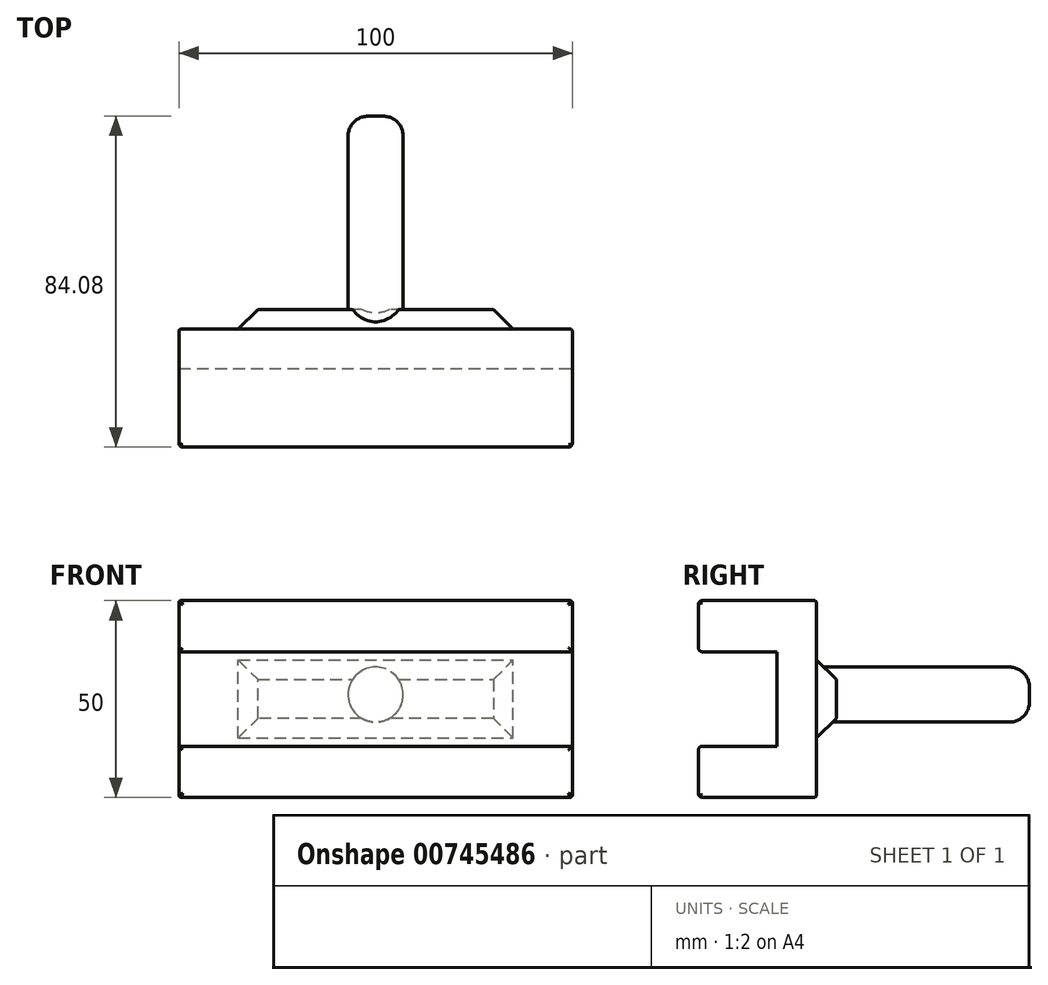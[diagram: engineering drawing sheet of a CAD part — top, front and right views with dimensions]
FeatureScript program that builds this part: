
annotation { "Feature Type Name" : "Feature", "Feature Type Description" : "" }
export const myFeature = defineFeature(function(context is Context, id is Id, definition is map)
    precondition{}
    {
        {
            var Q0;
            Q0=qCreatedBy(makeId("Front.planeOp"),FACE);
            var sketch = newSketch(context, id + "F0", { "sketchPlane" : qUnion([Q0])});
            skLineSegment(sketch, "E0.bottom", {"start": v(0, 0) * mm, "end": v(100, 0) * mm});
            skLineSegment(sketch, "E0.top", {"start": v(0, 50) * mm, "end": v(100, 50) * mm});
            skLineSegment(sketch, "E0.left", {"start": v(0, 0) * mm, "end": v(0, 50) * mm});
            skLineSegment(sketch, "E0.right", {"start": v(100, 0) * mm, "end": v(100, 50) * mm});
            skSolve(sketch);
        }
        {
            var Q0;
            Q0 = qSketchRegion(id + "F0", true);
            extrude(context, id + "F1", {"entities" : qUnion([Q0]), "depth" : 10 * mm, "offsetDistance" : 25.4 * mm});
        }
        {
            var Q0;
            Q0=makeQuery(id+"F1.opExtrude","CAP_FACE",FACE,{"disambiguationData":[OSD([sQuery(id+"F0.wireOp",EDGE,"E0.bottom"),sQuery(id+"F0.wireOp",EDGE,"E0.top"),sQuery(id+"F0.wireOp",EDGE,"E0.left"),sQuery(id+"F0.wireOp",EDGE,"E0.right")])],"isStart":false});
            var sketch = newSketch(context, id + "F2", { "sketchPlane" : qUnion([Q0])});
            skLineSegment(sketch, "E1.bottom", {"start": v(0, 50) * mm, "end": v(100, 50) * mm});
            skLineSegment(sketch, "E1.top", {"start": v(0, 37) * mm, "end": v(100, 37) * mm});
            skLineSegment(sketch, "E1.left", {"start": v(0, 50) * mm, "end": v(0, 37) * mm});
            skLineSegment(sketch, "E1.right", {"start": v(100, 50) * mm, "end": v(100, 37) * mm});
            skSolve(sketch);
        }
        {
            var Q0;
            Q0 = qSketchRegion(id + "F2", true);
            extrude(context, id + "F3", {"entities" : qUnion([Q0]), "operationType" : NewBodyOperationType.ADD, "depth" : 20 * mm, "offsetDistance" : 25.4 * mm});
        }
        {
            var Q0;
            Q0=makeQuery(id+"F1.opExtrude","CAP_FACE",FACE,{"disambiguationData":[OSD([sQuery(id+"F0.wireOp",EDGE,"E0.bottom"),sQuery(id+"F0.wireOp",EDGE,"E0.top"),sQuery(id+"F0.wireOp",EDGE,"E0.left"),sQuery(id+"F0.wireOp",EDGE,"E0.right")])],"isStart":false});
            var sketch = newSketch(context, id + "F4", { "sketchPlane" : qUnion([Q0])});
            skLineSegment(sketch, "E2.bottom", {"start": v(0, 0) * mm, "end": v(100, 0) * mm});
            skLineSegment(sketch, "E2.top", {"start": v(0, 13) * mm, "end": v(100, 13) * mm});
            skLineSegment(sketch, "E2.left", {"start": v(0, 0) * mm, "end": v(0, 13) * mm});
            skLineSegment(sketch, "E2.right", {"start": v(100, 0) * mm, "end": v(100, 13) * mm});
            skSolve(sketch);
        }
        {
            var Q0;
            Q0 = qSketchRegion(id + "F4", true);
            extrude(context, id + "F5", {"entities" : qUnion([Q0]), "operationType" : NewBodyOperationType.ADD, "depth" : 20 * mm, "offsetDistance" : 25.4 * mm});
        }
        {
            var Q0;
            Q0=makeQuery(id+"F1.opExtrude","CAP_FACE",FACE,{"disambiguationData":[OSD([sQuery(id+"F0.wireOp",EDGE,"E0.bottom"),sQuery(id+"F0.wireOp",EDGE,"E0.top"),sQuery(id+"F0.wireOp",EDGE,"E0.left"),sQuery(id+"F0.wireOp",EDGE,"E0.right")])],"isStart":true});
            var sketch = newSketch(context, id + "F6", { "sketchPlane" : qUnion([Q0])});
            skLineSegment(sketch, "E3.bottom", {"start": v(-85, 35) * mm, "end": v(-15, 35) * mm});
            skLineSegment(sketch, "E3.top", {"start": v(-85, 15) * mm, "end": v(-15, 15) * mm});
            skLineSegment(sketch, "E3.left", {"start": v(-85, 35) * mm, "end": v(-85, 15) * mm});
            skLineSegment(sketch, "E3.right", {"start": v(-15, 35) * mm, "end": v(-15, 15) * mm});
            skSolve(sketch);
        }
        {
            var Q0;
            Q0 = qSketchRegion(id + "F6", true);
            extrude(context, id + "F7", {"entities" : qUnion([Q0]), "operationType" : NewBodyOperationType.ADD, "depth" : 5 * mm, "offsetDistance" : 25.4 * mm});
        }
        {
            var Q0;
            Q0=makeQuery(id+"F7.opExtrude","CAP_FACE",FACE,{"disambiguationData":[OSD([sQuery(id+"F6.wireOp",EDGE,"E3.bottom"),sQuery(id+"F6.wireOp",EDGE,"E3.top"),sQuery(id+"F6.wireOp",EDGE,"E3.left"),sQuery(id+"F6.wireOp",EDGE,"E3.right")])],"isStart":false});
            var sketch = newSketch(context, id + "F8", { "sketchPlane" : qUnion([Q0])});
            skCircle(sketch, "E4", {"center": v(-50, 26.12) * mm, "radius": 7 * mm});
            skSolve(sketch);
        }
        {
            var Q0;
            Q0=makeQuery(id+"F8.imprint","IMPRINT",FACE,{"disambiguationData":[TD([[makeQuery(id+"F8.imprint","IMPRINT",EDGE,{"derivedFrom":sQuery(id+"F8.wireOp",EDGE,"E4")}),1.0]])]});
            extrude(context, id + "F9", {"entities" : qUnion([Q0]), "operationType" : NewBodyOperationType.ADD, "depth" : 49.08 * mm, "offsetDistance" : 25.4 * mm});
        }
        {
            var Q0;
            Q0=makeQuery(id+"F7.opExtrude","CAP_EDGE",EDGE,{"disambiguationData":[OSD([sQuery(id+"F6.wireOp",EDGE,"E3.top")])],"isStart":false});
            var Q1;
            Q1=makeQuery(id+"F7.opExtrude","CAP_EDGE",EDGE,{"disambiguationData":[OSD([sQuery(id+"F6.wireOp",EDGE,"E3.left")])],"isStart":false});
            var Q2;
            Q2=makeQuery(id+"F7.opExtrude","CAP_EDGE",EDGE,{"disambiguationData":[OSD([sQuery(id+"F6.wireOp",EDGE,"E3.bottom")])],"isStart":false});
            var Q3;
            Q3=makeQuery(id+"F7.opExtrude","CAP_EDGE",EDGE,{"disambiguationData":[OSD([sQuery(id+"F6.wireOp",EDGE,"E3.right")])],"isStart":false});
            chamfer(context, id + "F10", {"entities" : qUnion([Q0, Q1, Q2, Q3]), "width" : 5.08 * mm, "tangentPropagation" : true});
        }
        {
            var Q0;
            Q0=makeQuery(id+"F5.opExtrude","CAP_FACE",FACE,{"disambiguationData":[OSD([sQuery(id+"F4.wireOp",EDGE,"E2.bottom"),sQuery(id+"F4.wireOp",EDGE,"E2.top"),sQuery(id+"F4.wireOp",EDGE,"E2.left"),sQuery(id+"F4.wireOp",EDGE,"E2.right")])],"isStart":false});
            var Q1;
            Q1=makeQuery(id+"F3.opExtrude","CAP_FACE",FACE,{"disambiguationData":[OSD([sQuery(id+"F2.wireOp",EDGE,"E1.bottom"),sQuery(id+"F2.wireOp",EDGE,"E1.top"),sQuery(id+"F2.wireOp",EDGE,"E1.left"),sQuery(id+"F2.wireOp",EDGE,"E1.right")])],"isStart":false});
            fillet(context, id + "F11", {"entities" : qUnion([Q0, Q1]), "radius" : 1 * mm, "tangentPropagation" : true, "allowEdgeOverflow" : false});
        }
        {
            var Q0;
            Q0=makeQuery(id+"F5.boolean.opBoolean","MERGE",EDGE,{"derivedFrom":[makeQuery(id+"F1.opExtrude","SWEPT_EDGE",EDGE,{"disambiguationData":[OSD([sQuery(id+"F0.wireOp",EDGE,"E0.bottom"),sQuery(id+"F0.wireOp",EDGE,"E0.left")])]}),makeQuery(id+"F5.opExtrude","SWEPT_EDGE",EDGE,{"disambiguationData":[OSD([sQuery(id+"F4.wireOp",EDGE,"E2.bottom"),sQuery(id+"F4.wireOp",EDGE,"E2.left")])]})]});
            var Q1;
            Q1=makeQuery(id+"F3.boolean.opBoolean","MERGE",EDGE,{"derivedFrom":[makeQuery(id+"F1.opExtrude","SWEPT_EDGE",EDGE,{"disambiguationData":[OSD([sQuery(id+"F0.wireOp",EDGE,"E0.top"),sQuery(id+"F0.wireOp",EDGE,"E0.left")])]}),makeQuery(id+"F3.opExtrude","SWEPT_EDGE",EDGE,{"disambiguationData":[OSD([sQuery(id+"F2.wireOp",EDGE,"E1.bottom"),sQuery(id+"F2.wireOp",EDGE,"E1.left")])]})]});
            var Q2;
            Q2=makeQuery(id+"F1.opExtrude","CAP_EDGE",EDGE,{"disambiguationData":[OSD([sQuery(id+"F0.wireOp",EDGE,"E0.left")])],"isStart":true});
            var Q3;
            Q3=makeQuery(id+"F1.opExtrude","CAP_EDGE",EDGE,{"disambiguationData":[OSD([sQuery(id+"F0.wireOp",EDGE,"E0.bottom")])],"isStart":true});
            var Q4;
            Q4=makeQuery(id+"F5.boolean.opBoolean","MERGE",EDGE,{"derivedFrom":[makeQuery(id+"F1.opExtrude","SWEPT_EDGE",EDGE,{"disambiguationData":[OSD([sQuery(id+"F0.wireOp",EDGE,"E0.bottom"),sQuery(id+"F0.wireOp",EDGE,"E0.right")])]}),makeQuery(id+"F5.opExtrude","SWEPT_EDGE",EDGE,{"disambiguationData":[OSD([sQuery(id+"F4.wireOp",EDGE,"E2.bottom"),sQuery(id+"F4.wireOp",EDGE,"E2.right")])]})]});
            var Q5;
            Q5=makeQuery(id+"F1.opExtrude","CAP_EDGE",EDGE,{"disambiguationData":[OSD([sQuery(id+"F0.wireOp",EDGE,"E0.right")])],"isStart":true});
            var Q6;
            Q6=makeQuery(id+"F3.boolean.opBoolean","MERGE",EDGE,{"derivedFrom":[makeQuery(id+"F1.opExtrude","SWEPT_EDGE",EDGE,{"disambiguationData":[OSD([sQuery(id+"F0.wireOp",EDGE,"E0.top"),sQuery(id+"F0.wireOp",EDGE,"E0.right")])]}),makeQuery(id+"F3.opExtrude","SWEPT_EDGE",EDGE,{"disambiguationData":[OSD([sQuery(id+"F2.wireOp",EDGE,"E1.bottom"),sQuery(id+"F2.wireOp",EDGE,"E1.right")])]})]});
            var Q7;
            Q7=makeQuery(id+"F1.opExtrude","CAP_EDGE",EDGE,{"disambiguationData":[OSD([sQuery(id+"F0.wireOp",EDGE,"E0.top")])],"isStart":true});
            fillet(context, id + "F12", {"entities" : qUnion([Q0, Q1, Q2, Q3, Q4, Q5, Q6, Q7]), "radius" : 0.62 * mm, "tangentPropagation" : true, "allowEdgeOverflow" : false});
        }
        {
            var Q0;
            Q0=makeQuery(id+"F9.opExtrude","CAP_EDGE",EDGE,{"disambiguationData":[OSD([sQuery(id+"F8.wireOp",EDGE,"E4")])],"isStart":false});
            fillet(context, id + "F13", {"entities" : qUnion([Q0]), "radius" : 5.08 * mm, "tangentPropagation" : true, "allowEdgeOverflow" : false});
        }
    });
